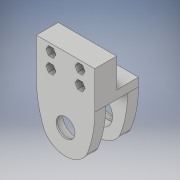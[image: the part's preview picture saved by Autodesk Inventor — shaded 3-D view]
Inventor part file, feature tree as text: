
AUTODESK INVENTOR PART (.ipt)
format: ipt  version: 2019 (Build 230136000, 136)  size: 321,536 bytes
history: native  units: mm
features: sketch x13, extrude x10, chamfer x5, hole x3, plane x1, fillet x1, draft x1
ambient origin geometry x8: Origin, YZ Plane, XZ Plane, XY Plane, X Axis, Y Axis, Z Axis, Center Point
bodies: Solid1 (feature_tree)
feature tree (34):
  extrude  "Extrusion1"  Depth=20.0mm
  extrude  "Extrusion2"  Depth=40.0mm
  hole  "Hole1"  [1 undecoded]
  plane  "Work Plane1"
  extrude  "Extrusion3"  Depth=30.0mm TaperAngle=360.0deg
  extrude  "Extrusion4"  Depth=15.0mm TaperAngle=0.0deg
  hole  "Hole2"  [1 undecoded]
  extrude  "Extrusion5"  Depth=10.0mm
  extrude  "Extrusion6"  Depth=5.9mm
  chamfer  "Chamfer2"  Distance=3.5mm
  fillet  "Fillet1"  Radius=17.0mm
  extrude  "Extrusion7"  Depth=10.0mm TaperAngle=45.0deg
  chamfer  "Chamfer3"  Distance=10.0mm
  chamfer  "Chamfer4"  Distance=9.17mm Angle=45.0deg
  extrude  "Extrusion8"  Depth=3.5mm TaperAngle=45.0deg
  extrude  "Extrusion9"  Depth=3.5mm TaperAngle=0.0deg
  hole  "Hole3"  [1 undecoded]
  extrude  "Extrusion10"  Depth=3.5mm
  chamfer  "Chamfer6"  Distance=10.0mm
  chamfer  "Chamfer7"  Distance=4.66mm Angle=45.0deg
  draft  "FaceDraft1"
  sketch  "Sketch1"  dims[d0=19.5mm d2=20.0mm]
  sketch  "Sketch2"  dims[d3=45.0mm d4=40.0mm]
  sketch  "Sketch3"  dims[d5=30.0mm d6=0.0mm d7=27.0mm]
  sketch  "Sketch4"  dims[d8=7.0mm d9=30.0mm d11=360.0deg]
  sketch  "Sketch5"  dims[d13=3.5mm d14=0.0mm]
  sketch  "Sketch6"  dims[d15=4.8mm d16=6.0mm d17=6.5mm d18=5.0mm d19=14.835299mm d20=6.0mm d21=90.0deg d22=15.0mm d23=0.0mm]
  sketch  "Sketch7"  dims[d27=20.0mm d28=15.0mm d29=0.0mm]
  sketch  "Sketch8"  dims[d30=20.0mm]
  sketch  "Sketch10"  dims[d31=3.75mm d32=6.0mm d33=4.0mm d34=2.0mm d35=90.0deg d36=10.0mm d37=90.0deg d38=5.9mm]
  sketch  "Sketch11"  dims[d39=5.9mm d40=5.9mm]
  sketch  "Sketch12"  dims[d41=5.9mm d42=3.5mm d43=0.0mm d44=17.0mm]
  sketch  "Sketch13"  dims[d45=10.0mm d46=0.0mm d47=8.25mm d48=2.0mm d49=45.0deg]
  sketch  "Sketch14"  dims[d50=74.25mm d51=10.0mm d52=0.0mm d53=9.17mm d54=2.0mm d55=45.0deg d56=4.0mm d57=2.0mm d58=45.0deg d59=1.0mm d60=0.0mm d61=1.0mm d62=0.0mm d66=13.0mm d67=6.0mm d68=10.0mm d69=7.0mm d70=90.0deg d71=8.0mm d72=20.594885mm d73=1.5mm d74=10.0mm d75=0.0mm d76=4.66mm d77=2.0mm d78=45.0deg d79=3.5mm d80=2.0mm d81=45.0deg d82=45.0deg]
note: 3 required parameter values undecoded (feature->parameter linkage not recoverable at this tier; creation-order binding heuristic only, values carry confidence <= 0.55)
